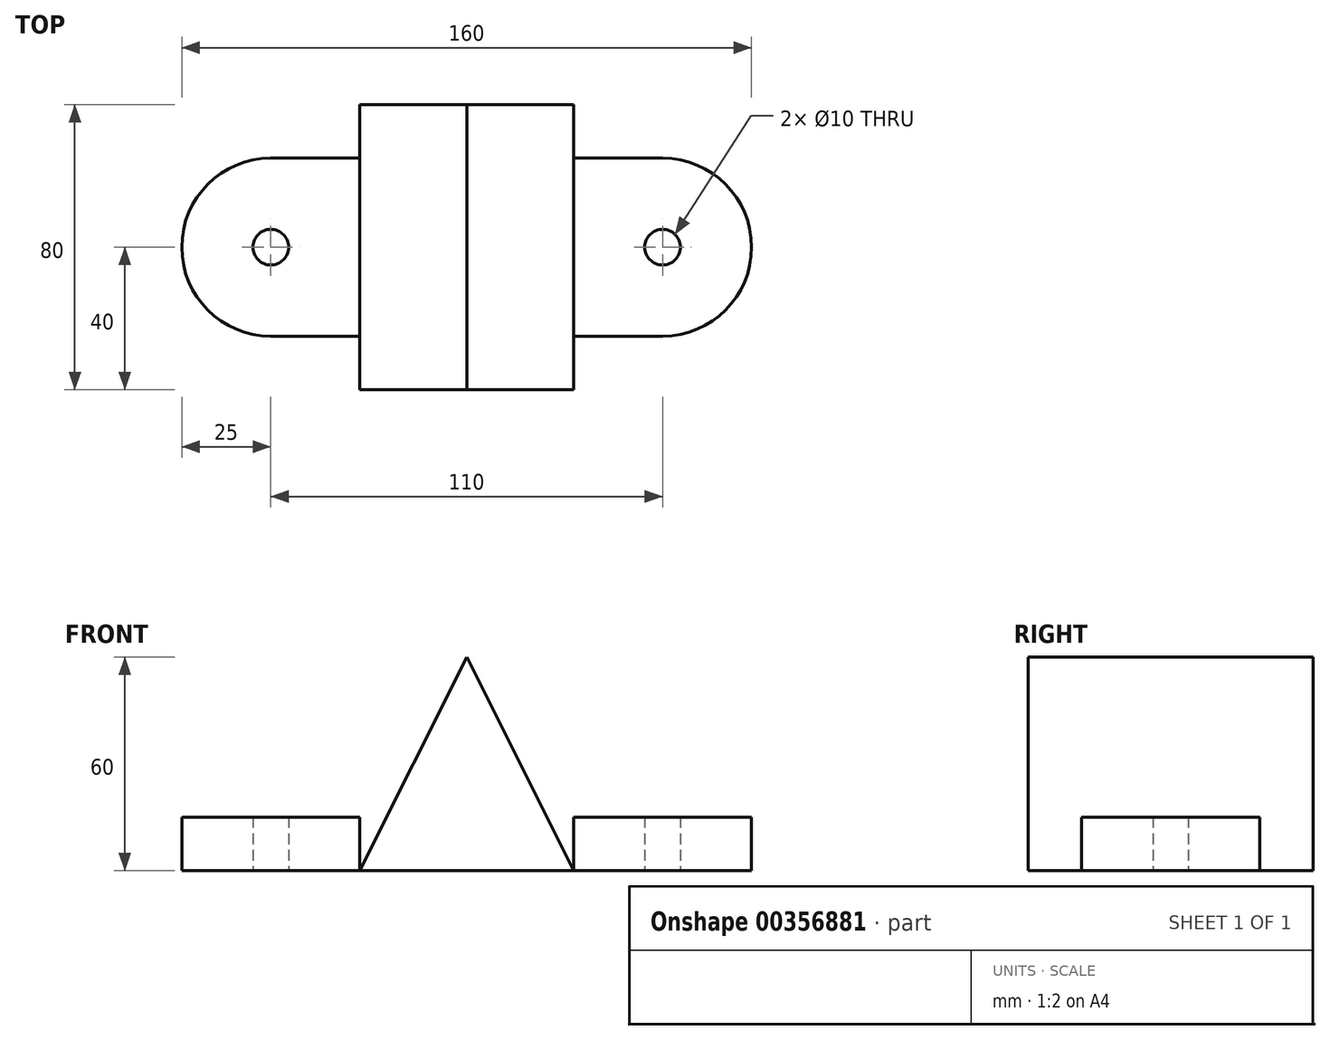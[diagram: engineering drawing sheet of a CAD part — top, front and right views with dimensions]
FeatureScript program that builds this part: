
annotation { "Feature Type Name" : "Feature", "Feature Type Description" : "" }
export const myFeature = defineFeature(function(context is Context, id is Id, definition is map)
    precondition{}
    {
        {
            var Q0;
            Q0=qCreatedBy(makeId("Top.planeOp"),FACE);
            var sketch = newSketch(context, id + "F0", { "sketchPlane" : qUnion([Q0])});
            skLineSegment(sketch, "E0", {"start": v(0, 0) * mm, "end": v(-55, 0) * mm});
            skCircle(sketch, "E1", {"center": v(-55, 0) * mm, "radius": 5 * mm});
            skArc(sketch, "E2", {"start": v(-55, 25) * mm, "mid": v(-80, 0) * mm, "end": v(-55, -25) * mm});
            skLineSegment(sketch, "E3", {"start": v(-55, 25) * mm, "end": v(-30, 25) * mm});
            skLineSegment(sketch, "E4", {"start": v(-55, -25) * mm, "end": v(-30, -25) * mm});
            skLineSegment(sketch, "E5", {"start": v(-30, 40) * mm, "end": v(-30, -40) * mm});
            skLineSegment(sketch, "E6", {"start": v(-30, 40) * mm, "end": v(0, 40) * mm});
            skLineSegment(sketch, "E7", {"start": v(-30, -40) * mm, "end": v(0, -40) * mm});
            skLineSegment(sketch, "E8.MirrorCS", {"start": v(30, 40) * mm, "end": v(0, 40) * mm});
            skLineSegment(sketch, "E9.MirrorCS", {"start": v(30, 40) * mm, "end": v(30, -40) * mm});
            skLineSegment(sketch, "E10.MirrorCS", {"start": v(55, 25) * mm, "end": v(30, 25) * mm});
            skArc(sketch, "E11.MirrorCS", {"start": v(55, 25) * mm, "mid": v(80, 0) * mm, "end": v(55, -25) * mm});
            skLineSegment(sketch, "E12.MirrorCS", {"start": v(55, -25) * mm, "end": v(30, -25) * mm});
            skLineSegment(sketch, "E13.MirrorCS", {"start": v(30, -40) * mm, "end": v(0, -40) * mm});
            skCircle(sketch, "E14.MirrorC", {"center": v(55, 0) * mm, "radius": 5 * mm});
            skSolve(sketch);
        }
        {
            var Q0;
            Q0=makeQuery(id+"F0.imprint","IMPRINT",FACE,{"disambiguationData":[TD([[makeQuery(id+"F0.imprint","IMPRINT",EDGE,{"derivedFrom":sQuery(id+"F0.wireOp",EDGE,"E1")}),-1.0]])]});
            var Q1;
            {var subQ6=sQuery(id+"F0.wireOp",EDGE,"E6");Q1=makeQuery(id+"F0.imprint","IMPRINT",FACE,{"disambiguationData":[TD([[makeQuery(id+"F0.imprint","IMPRINT",EDGE,{"derivedFrom":subQ6}),-1.0]])]});}
            var Q2;
            {var subQ1=sQuery(id+"F0.wireOp",EDGE,"E10.MirrorCS");Q2=makeQuery(id+"F0.imprint","IMPRINT",FACE,{"disambiguationData":[TD([[makeQuery(id+"F0.imprint","IMPRINT",EDGE,{"derivedFrom":subQ1}),1.0]])]});}
            extrude(context, id + "F1", {"entities" : qUnion([Q0, Q1, Q2]), "depth" : 60 * mm});
        }
        {
            var Q0;
            Q0=makeQuery(id+"F1.opExtrude","CAP_FACE",FACE,{"disambiguationData":[OSD([sQuery(id+"F0.wireOp",EDGE,"E1"),sQuery(id+"F0.wireOp",EDGE,"E2"),sQuery(id+"F0.wireOp",EDGE,"E3"),sQuery(id+"F0.wireOp",EDGE,"E4"),sQuery(id+"F0.wireOp",EDGE,"E5"),sQuery(id+"F0.wireOp",EDGE,"E6"),sQuery(id+"F0.wireOp",EDGE,"E7"),sQuery(id+"F0.wireOp",EDGE,"E8.MirrorCS"),sQuery(id+"F0.wireOp",EDGE,"E9.MirrorCS"),sQuery(id+"F0.wireOp",EDGE,"E10.MirrorCS"),sQuery(id+"F0.wireOp",EDGE,"E11.MirrorCS"),sQuery(id+"F0.wireOp",EDGE,"E12.MirrorCS"),sQuery(id+"F0.wireOp",EDGE,"E13.MirrorCS"),sQuery(id+"F0.wireOp",EDGE,"E14.MirrorC")])],"isStart":false});
            extrude(context, id + "F2", {"entities" : qUnion([Q0]), "operationType" : NewBodyOperationType.REMOVE, "oppositeDirection" : true, "depth" : 45 * mm});
        }
        {
            var Q0;
            Q0=makeQuery(id+"F2.boolean.opBoolean","COPY",FACE,{"derivedFrom":makeQuery(id+"F2.opExtrude","CAP_FACE",FACE,{"disambiguationData":[OSD([sQuery(id+"F0.wireOp",EDGE,"E1"),sQuery(id+"F0.wireOp",EDGE,"E2"),sQuery(id+"F0.wireOp",EDGE,"E3"),sQuery(id+"F0.wireOp",EDGE,"E4"),sQuery(id+"F0.wireOp",EDGE,"E5"),sQuery(id+"F0.wireOp",EDGE,"E6"),sQuery(id+"F0.wireOp",EDGE,"E7"),sQuery(id+"F0.wireOp",EDGE,"E8.MirrorCS"),sQuery(id+"F0.wireOp",EDGE,"E9.MirrorCS"),sQuery(id+"F0.wireOp",EDGE,"E10.MirrorCS"),sQuery(id+"F0.wireOp",EDGE,"E11.MirrorCS"),sQuery(id+"F0.wireOp",EDGE,"E12.MirrorCS"),sQuery(id+"F0.wireOp",EDGE,"E13.MirrorCS"),sQuery(id+"F0.wireOp",EDGE,"E14.MirrorC")])],"isStart":false})});
            var sketch = newSketch(context, id + "F3", { "sketchPlane" : qUnion([Q0])});
            skLineSegment(sketch, "E15", {"start": v(-30, 40) * mm, "end": v(-30, -40) * mm});
            skLineSegment(sketch, "E16", {"start": v(-30, 40) * mm, "end": v(30, 40) * mm});
            skLineSegment(sketch, "E17", {"start": v(30, 40) * mm, "end": v(30, -40) * mm});
            skLineSegment(sketch, "E18", {"start": v(-30, -40) * mm, "end": v(30, -40) * mm});
            skSolve(sketch);
        }
        {
            var Q0;
            {var subQ0=sQuery(id+"F3.wireOp",EDGE,"E16");Q0=makeQuery(id+"F3.imprint","IMPRINT",FACE,{"disambiguationData":[TD([[makeQuery(id+"F3.imprint","IMPRINT",EDGE,{"derivedFrom":subQ0}),1.0]])]});}
            extrude(context, id + "F4", {"entities" : qUnion([Q0]), "operationType" : NewBodyOperationType.ADD, "depth" : 45 * mm});
        }
        {
            var Q0;
            Q0=makeQuery(id+"F4.boolean.opBoolean","MERGE",FACE,{"derivedFrom":[makeQuery(id+"F1.opExtrude","SWEPT_FACE",FACE,{"disambiguationData":[OSD([sQuery(id+"F0.wireOp",EDGE,"E7"),sQuery(id+"F0.wireOp",EDGE,"E13.MirrorCS")])]}),makeQuery(id+"F4.opExtrude","SWEPT_FACE",FACE,{"disambiguationData":[OSD([sQuery(id+"F3.wireOp",EDGE,"E18")])]})]});
            var sketch = newSketch(context, id + "F5", { "sketchPlane" : qUnion([Q0])});
            skLineSegment(sketch, "E19", {"start": v(-30, 0) * mm, "end": v(0, 60) * mm});
            skLineSegment(sketch, "E20", {"start": v(0, 60) * mm, "end": v(30, 0) * mm});
            skLineSegment(sketch, "E21", {"start": v(30, 0) * mm, "end": v(-30, 0) * mm});
            skSolve(sketch);
        }
        {
            var Q0;
            {var subQ0=sQuery(id+"F5.wireOp",EDGE,"E19");Q0=makeQuery(id+"F5.imprint","IMPRINT",FACE,{"disambiguationData":[TD([[makeQuery(id+"F5.imprint","IMPRINT",EDGE,{"derivedFrom":subQ0}),1.0]])]});}
            var Q1;
            {var subQ0=sQuery(id+"F5.wireOp",EDGE,"E20");Q1=makeQuery(id+"F5.imprint","IMPRINT",FACE,{"disambiguationData":[TD([[makeQuery(id+"F5.imprint","IMPRINT",EDGE,{"derivedFrom":subQ0}),1.0]])]});}
            extrude(context, id + "F6", {"entities" : qUnion([Q0, Q1]), "operationType" : NewBodyOperationType.REMOVE, "oppositeDirection" : true, "depth" : 80 * mm});
        }
    });
